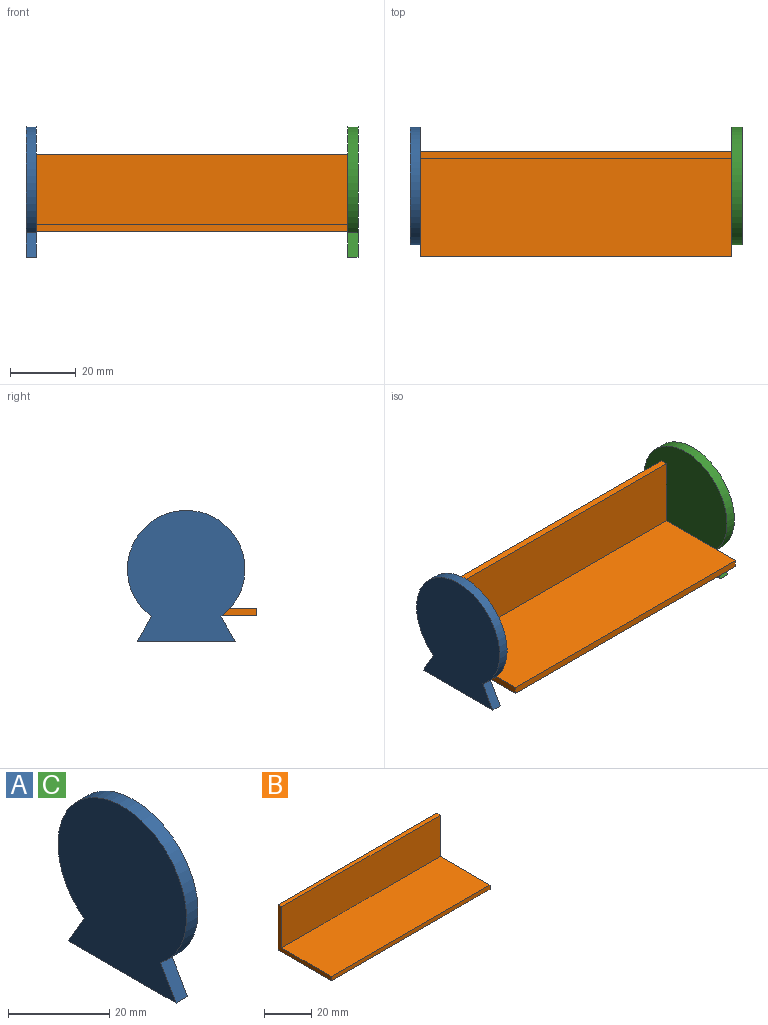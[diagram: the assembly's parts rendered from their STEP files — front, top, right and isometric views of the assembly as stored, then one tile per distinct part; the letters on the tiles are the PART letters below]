
ASSEMBLY  parts=3 mates=2
PART A: 6 faces, bbox 3.2x35.9x40 mm
  f0: plane 30x3.2mm, normal (0,0,-1), area 96mm2, adj f1,f3,f4,f5
  f1: plane 7.6x4.39mm, normal (0,0.87,0.5), area 28.1mm2, adj f0,f2,f4,f5
  f2: cylinder r=17.94mm len=35.88mm, axis (-1,0,0), area 288mm2, adj f1,f3,f4,f5
  f3: plane 7.6x4.39mm, normal (0,-0.87,0.5), area 28.1mm2, adj f0,f2,f4,f5
  f4: plane 40x35.88mm, normal (1,0,0), area 1155.3mm2, adj f0,f1,f2,f3
  f5: plane 40x35.88mm, normal (-1,0,0), area 1155.3mm2, adj f0,f1,f2,f3
PART B: 8 faces, bbox 95x32x23.5 mm
  f0: plane 95x32mm, normal (0,0,-1), area 3040mm2, adj f1,f5,f6,f7
  f1: plane 95x23.5mm, normal (0,1,0), area 2232.5mm2, adj f0,f2,f6,f7
  f2: plane 95x2.2mm, normal (0,0,1), area 209mm2, adj f1,f3,f6,f7
  f3: plane 95x21.3mm, normal (0,-1,0), area 2023.5mm2, adj f2,f4,f6,f7
  f4: plane 95x29.8mm, normal (0,0,1), area 2831mm2, adj f3,f5,f6,f7
  f5: plane 95x2.2mm, normal (0,-1,0), area 209mm2, adj f0,f4,f6,f7
  f6: plane 32x23.5mm, normal (1,0,0), area 117.3mm2, adj f0,f1,f2,f3,f4,f5
  f7: plane 32x23.5mm, normal (-1,0,0), area 117.3mm2, adj f0,f1,f2,f3,f4,f5
PART C: same geometry as A
PLACE A t=(-0.05,-0.61,-0.39)mm
PLACE B t=(50.65,9.93,7.46)mm
PLACE C t=(98.05,-0.61,-0.39)mm
MATE pin_slot C.f2 <-> A.f2  axis (-1,0,0) through (99.65,-0.61,21.68)mm
MATE slider A.f4 <-> B.f7  axis (1,0,0) through (3.15,-0.61,19.25)mm
